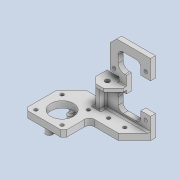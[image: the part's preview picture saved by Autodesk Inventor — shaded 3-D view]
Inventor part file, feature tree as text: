
AUTODESK INVENTOR PART (.ipt)
format: ipt  version: 2020 (Build 240168000, 168)  size: 572,416 bytes
history: native  units: mm
features: extrude x17, sketch x17, projected_geometry x17, fillet x12, reference x11, thicken_offset x10, other x8, chamfer x7
ambient origin geometry x8: Origin, YZ Plane, XZ Plane, XY Plane, X Axis, Y Axis, Z Axis, Center Point
bodies: Solid1 (feature_tree)
feature tree (99):
  extrude  "Extrusion1"  Depth=15.0mm
  extrude  "Extrusion2"  Depth=2.0mm
  extrude  "Extrusion3"  Depth=8.0mm
  extrude  "Extrusion4"  Depth=1.0mm
  extrude  "Extrusion5"  Depth=2.0mm
  extrude  "Extrusion6"  Depth=5.0mm
  fillet  "Fillet1"  Radius=3.85mm
  thicken_offset  "Thicken1"
  extrude  "Extrusion7"  Depth=8.0mm
  fillet  "Fillet3"  Radius=8.0mm
  extrude  "Extrusion8"  Depth=10.0mm TaperAngle=0.0deg
  thicken_offset  "Thicken2"
  thicken_offset  "Thicken3"
  extrude  "Extrusion9"  Depth=3.85mm
  extrude  "Extrusion10"  Depth=10.0mm TaperAngle=0.0deg
  extrude  "Extrusion11"  Depth=4.0mm
  extrude  "Extrusion12"  Depth=5.0mm
  chamfer  "Chamfer1"  Distance=5.0mm
  thicken_offset  "Thicken4"
  chamfer  "Chamfer2"  Distance=9.0mm
  extrude  "Extrusion13"  Depth=25.0mm
  thicken_offset  "Thicken5"
  thicken_offset  "Thicken6"
  extrude  "Extrusion14"  Depth=5.0mm
  thicken_offset  "Thicken7"
  thicken_offset  "Thicken8"
  fillet  "Fillet4"  Radius=6.0mm
  fillet  "Fillet5"  Radius=7.0mm
  extrude  "Extrusion15"  Depth=3.0mm TaperAngle=0.0deg
  chamfer  "Chamfer3"  Distance=3.0mm
  extrude  "Extrusion16"  Depth=4.0mm
  extrude  "Extrusion17"  Depth=50.0mm
  fillet  "Fillet6"  Radius=3.0mm
  fillet  "Fillet7"  Radius=30.0mm
  fillet  "Fillet8"  Radius=3.0mm
  chamfer  "Chamfer4"  Distance=3.0mm
  fillet  "Fillet9"  Radius=1.0mm
  fillet  "Fillet10"  Radius=1.0mm
  chamfer  "Chamfer5"  Distance=30.0mm
  fillet  "Fillet11"  Radius=16.0mm
  thicken_offset  "Thicken9"
  thicken_offset  "Thicken10"
  fillet  "Fillet12"  Radius=12.0mm
  chamfer  "Chamfer6"  Distance=14.0mm
  chamfer  "Chamfer7"  Distance=30.0mm
  fillet  "Fillet13"  Radius=2.0mm
  sketch  "Sketch1"  dims[d0=5.0mm d1=15.0mm]
  reference  "Reference1"
  reference  "Reference2"
  sketch  "Sketch2"  dims[d2=3.0mm d3=0.0mm d4=2.0mm]
  projected_geometry  "Projected Loop1"
  sketch  "Sketch3"  dims[d5=6.0mm d6=8.0mm]
  projected_geometry  "Projected Loop2"
  sketch  "Sketch4"  dims[d7=3.0mm d8=0.0mm d9=1.0mm]
  reference  "Reference3"
  projected_geometry  "Projected Loop3"
  projected_geometry  "Projected Loop4"
  projected_geometry  "Projected Loop5"
  sketch  "Sketch5"  dims[d10=10.0mm d11=2.0mm]
  reference  "Reference4"
  sketch  "Sketch6"  dims[d12=10.0mm d13=0.0mm d14=5.0mm d15=3.85mm]
  projected_geometry  "Projected Loop6"
  projected_geometry  "Projected Loop7"
  sketch  "Sketch7"  dims[d16=3.0mm d17=8.0mm d18=8.0mm]
  reference  "Reference5"
  reference  "Reference6"
  sketch  "Sketch8"  dims[d19=11.9mm d20=10.0mm d21=0.0mm]
  projected_geometry  "Projected Loop8"
  sketch  "Sketch9"  dims[d22=5.0mm d23=3.85mm]
  projected_geometry  "Projected Loop9"
  sketch  "Sketch10"  dims[d24=2.8mm d25=10.0mm d26=0.0mm]
  projected_geometry  "Projected Loop10"
  reference  "Reference7"
  sketch  "Sketch11"  dims[d27=2.5mm d28=0.0mm d29=4.0mm]
  projected_geometry  "Projected Loop11"
  sketch  "Sketch12"  dims[d31=1.1mm d32=1.0mm d33=5.0mm]
  projected_geometry  "Projected Loop12"
  sketch  "Sketch13"  dims[d34=9.0mm]
  reference  "Reference8"
  reference  "Reference9"
  reference  "Reference10"
  reference  "Reference11"
  sketch  "Sketch14"  dims[d35=25.0mm]
  projected_geometry  "Projected Loop13"
  sketch  "Sketch15"  dims[d36=5.0mm]
  projected_geometry  "Projected Loop14"
  sketch  "Sketch16"  dims[d37=6.0mm]
  projected_geometry  "Projected Loop15"
  projected_geometry  "Projected Loop16"
  sketch  "Sketch17"  dims[d38=7.0mm d39=5.0mm d40=9.0mm d41=25.0mm d42=5.0mm d43=6.0mm d44=7.0mm d45=3.0mm d46=0.0mm d47=3.0mm d48=4.0mm d49=50.0mm d50=3.0mm d51=30.0mm d52=0.0mm d53=3.0mm d54=3.0mm d55=1.0mm d56=1.0mm d57=30.0mm d58=0.0mm d59=16.0mm d60=12.0mm d61=14.0mm d62=30.0mm d63=0.0mm d64=2.0mm d65=17.5mm d66=30.0mm d67=0.0mm d68=30.0mm d69=0.0mm d70=10.0mm d71=2.0mm d72=45.0deg d73=4.0mm d74=4.0mm d75=7.0mm d76=2.0mm d77=45.0deg d78=30.0mm d79=0.0mm d80=2.0mm d81=2.0mm d82=2.0mm d83=2.0mm d84=30.0mm d85=0.0mm d86=1.0mm d87=1.0mm d88=0.5mm d89=0.5mm d90=0.5mm d91=1.0mm d92=5.5mm d93=5.5mm d94=2.5mm d95=4.0mm d96=2.5mm d97=4.0mm d98=4.3mm d99=0.0mm d100=1.0mm d101=2.0mm d102=45.0deg d103=1.8mm d104=1.8mm d105=4.0mm d106=0.0mm d107=6.0mm d108=10.0mm d109=2.0mm d110=2.0mm d111=4.0mm d112=0.0mm d113=1.0mm d114=1.0mm d115=3.0mm d116=6.0mm d117=2.0mm d118=45.0deg d119=0.5mm d120=2.0mm d121=2.0mm d122=2.0mm d123=45.0deg d124=3.0mm d125=1.0mm d126=1.0mm d127=1.0mm d128=1.0mm d129=1.0mm d130=4.0mm d131=2.0mm d132=45.0deg d133=4.0mm d134=2.0mm d135=45.0deg d136=0.5mm]
  projected_geometry  "Projected Loop17"
  parser-record x1  (decoder bookkeeping rows leaked as tree rows — omitted from the tree; the rows remain in map.json)
  other  "tip_3_n_base_ass.iam"
  other  "ext_pin_shell_2:1"
  other  "bl_tube_ass_2:1"
  other  "bl_tube_hn_1:1"
  other  "bearing_3_6_2:5"
  other  "mot_27_ass:2"
  other  "mot_27_2:1"
note: 1 file-system path scrubbed to <path> (originals preserved in map.json)
